# Revit family: Toilet Roll Dispenser_Metlam_Double_Cabinet_Rectangular
name_source: partatom
category: Specialty Equipment
revit_build: Autodesk Revit 2016 (Build: 20170117_1200(x64)
units: mm (PartAtom-declared; Revit-internal decimal feet)

## family parameters
Always vertical = Yes
Cut with Voids When Loaded = No
OmniClass Number = 23.40.20.21.21
OmniClass Title = Toilet Paper Dispensers
Part Type = Normal
Room Calculation Point = Yes
Round Connector Dimension = Use Diameter
Shared = No
Work Plane-Based = No

## types (2) — shared parameters
Manufacturer = Metlam
Manufacturer_Overall Depth = 126 mm  [stored 0.413386 ft]
Manufacturer_Overall Height = 310 mm  [stored 1.01706 ft]
Manufacturer_Overall Width = 118 mm
Manufacturer_URL__Product Specific = https://metlam.com.au
Type Comments = Toilet Roll Dispensers
URL = http://www.metlam.com.au

## per-type parameters (varying)
| type | Description | Manufacturer_Spec Code | Material_ANZRS | Model |
| Satin 118w x 126d x 310h (ML832SS) | Double Toilet Roll Dispenser - SS Satin Finish | ML832SS | z_Metlam_Metal_Stainless Steel_Satin | ML832SS |
| White 118w x 126d x 310h (ML832W) | Double Toilet Roll Dispenser - White Powder Coat | ML832W | z_Metlam_White | ML832W |

note: [stored X ft] marks values corroborated as IEEE doubles in the binary element streams (Revit-internal decimal feet)

## geometry (parser evidence)
native form markers: Sweep x3
no freeform markers — native parametric forms only
